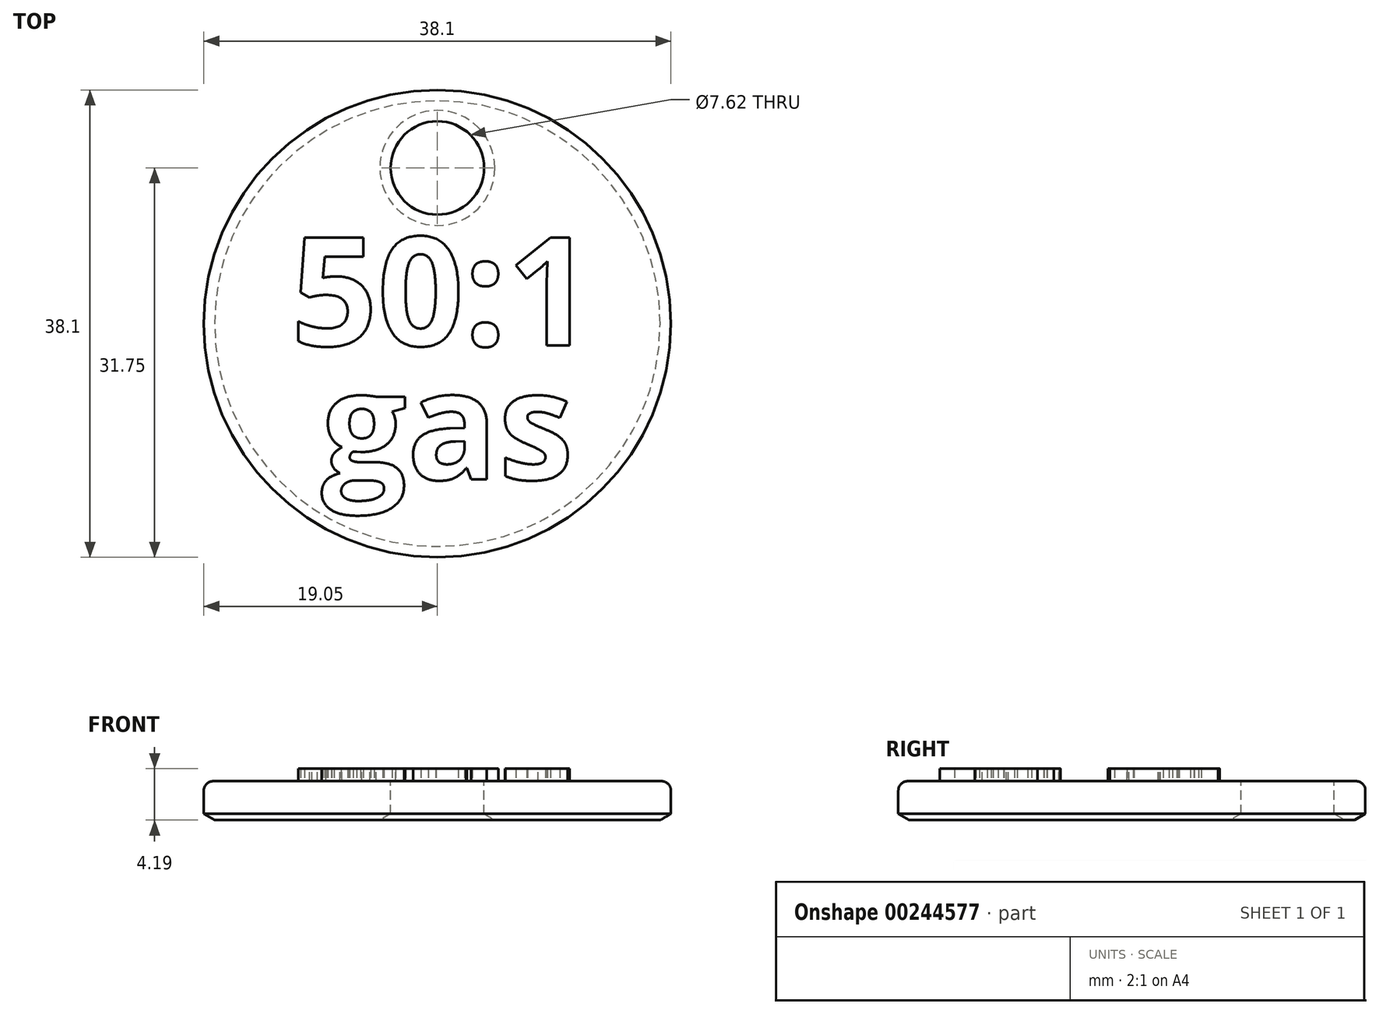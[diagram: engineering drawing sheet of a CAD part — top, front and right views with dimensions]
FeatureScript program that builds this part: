
annotation { "Feature Type Name" : "Feature", "Feature Type Description" : "" }
export const myFeature = defineFeature(function(context is Context, id is Id, definition is map)
    precondition{}
    {
        {
            var Q0;
            Q0=qCreatedBy(makeId("Top.planeOp"),FACE);
            var sketch = newSketch(context, id + "F0", { "sketchPlane" : qUnion([Q0])});
            skCircle(sketch, "E0", {"center": v(0, 0) * mm, "radius": 19.05 * mm});
            skSolve(sketch);
        }
        {
            var Q0;
            Q0=makeQuery(id+"F0.imprint","IMPRINT",FACE,{"disambiguationData":[TD([[makeQuery(id+"F0.imprint","IMPRINT",EDGE,{"derivedFrom":sQuery(id+"F0.wireOp",EDGE,"E0")}),1.0]])]});
            extrude(context, id + "F1", {"entities" : qUnion([Q0]), "depth" : 3.17 * mm});
        }
        {
            var Q0;
            Q0=makeQuery(id+"F1.opExtrude","CAP_FACE",FACE,{"disambiguationData":[OSD([sQuery(id+"F0.wireOp",EDGE,"E0")])],"isStart":false});
            var sketch = newSketch(context, id + "F2", { "sketchPlane" : qUnion([Q0])});
            skText(sketch, "E1", { "text": "50:1", "fontName": "OpenSans-Bold.ttf"});
            skText(sketch, "E2", { "text": "gas", "fontName": "OpenSans-Bold.ttf"});
            const initialGuessF2  = {"E1": [-0.01194, -0.00178, 1, 0, 0.00889], "E2": [-0.00947, -0.0127, 1, 0, 0.00889]};
            skSetInitialGuess(sketch, initialGuessF2);
            skSolve(sketch);
        }
        {
            var Q0;
            Q0=qSketchRegion(id+"F2",true);
            extrude(context, id + "F3", {"entities" : qUnion([Q0]), "operationType" : NewBodyOperationType.ADD, "depth" : 1.02 * mm});
        }
        {
            var Q0;
            {var subQ0=sQuery(id+"F0.wireOp",EDGE,"E0");Q0=makeQuery(id+"F3.boolean.opBoolean","SPLIT",FACE,{"disambiguationData":[TD([makeQuery(id+"F1.opExtrude","SWEPT_FACE",FACE,{"disambiguationData":[OSD([subQ0])]})])],"derivedFrom":makeQuery(id+"F1.opExtrude","CAP_FACE",FACE,{"disambiguationData":[OSD([subQ0])],"isStart":false})});}
            var sketch = newSketch(context, id + "F4", { "sketchPlane" : qUnion([Q0])});
            skCircle(sketch, "E3", {"center": v(0, 12.7) * mm, "radius": 3.81 * mm});
            skSolve(sketch);
        }
        {
            var Q0;
            Q0=qSketchRegion(id+"F4",true);
            extrude(context, id + "F5", {"entities" : qUnion([Q0]), "operationType" : NewBodyOperationType.REMOVE, "endBound" : BoundingType.UP_TO_NEXT, "oppositeDirection" : true, "depth" : 25.4 * mm});
        }
        {
            var Q0;
            Q0=makeQuery(id+"F1.opExtrude","CAP_EDGE",EDGE,{"disambiguationData":[OSD([sQuery(id+"F0.wireOp",EDGE,"E0")])],"isStart":false});
            var Q1;
            Q1=makeQuery(id+"F5.boolean.opBoolean","COPY",EDGE,{"derivedFrom":makeQuery(id+"F5.opExtrude","CAP_EDGE",EDGE,{"disambiguationData":[OSD([sQuery(id+"F4.wireOp",EDGE,"E3")])],"isStart":true})});
            fillet(context, id + "F6", {"entities" : qUnion([Q0, Q1]), "radius" : 0.76 * mm, "tangentPropagation" : true, "allowEdgeOverflow" : false});
        }
        {
            var Q0;
            Q0=makeQuery(id+"F1.opExtrude","CAP_FACE",FACE,{"disambiguationData":[OSD([sQuery(id+"F0.wireOp",EDGE,"E0")])],"isStart":true});
            chamfer(context, id + "F7", {"entities" : qUnion([Q0]), "chamferType" : ChamferType.OFFSET_ANGLE, "width" : 0.5 * mm, "oppositeDirection" : false, "angle" : 60 * degree, "tangentPropagation" : true});
        }
    });
